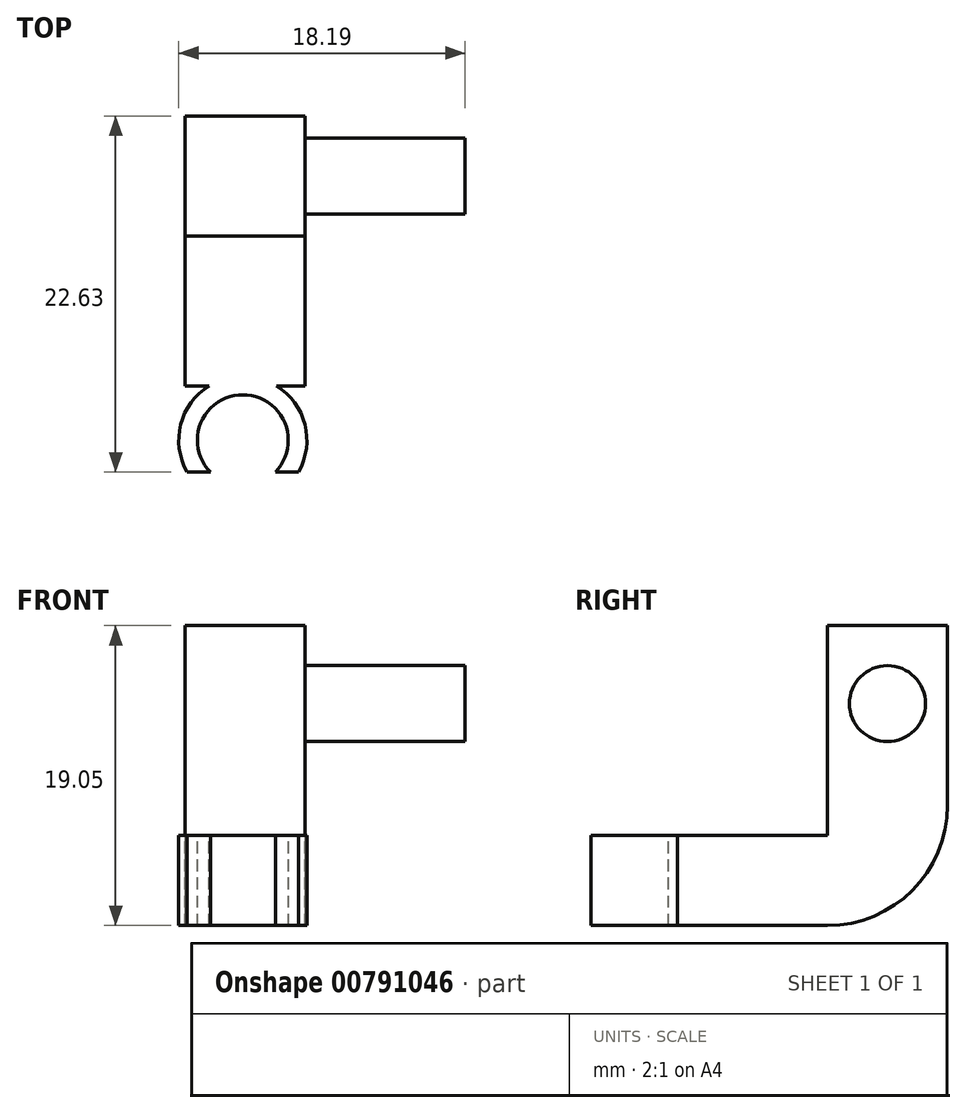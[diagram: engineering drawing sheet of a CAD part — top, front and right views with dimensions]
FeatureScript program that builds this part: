
annotation { "Feature Type Name" : "Feature", "Feature Type Description" : "" }
export const myFeature = defineFeature(function(context is Context, id is Id, definition is map)
    precondition{}
    {
        {
            var Q0;
            Q0=qCreatedBy(makeId("Front.planeOp"),FACE);
            var sketch = newSketch(context, id + "F0", { "sketchPlane" : qUnion([Q0])});
            skLineSegment(sketch, "E0.bottom", {"start": v(0, 26.58) * mm, "end": v(5.08, 26.58) * mm});
            skLineSegment(sketch, "E0.top", {"start": v(0, 13.88) * mm, "end": v(5.08, 13.88) * mm});
            skLineSegment(sketch, "E0.left", {"start": v(0, 26.58) * mm, "end": v(0, 13.88) * mm});
            skLineSegment(sketch, "E0.right", {"start": v(5.08, 26.58) * mm, "end": v(5.08, 13.88) * mm});
            skSolve(sketch);
        }
        {
            var Q0;
            Q0 = qSketchRegion(id + "F0", true);
            extrude(context, id + "F1", {"entities" : qUnion([Q0]), "depth" : 5.08 * mm, "offsetDistance" : 25.4 * mm});
        }
        {
            var Q0;
            Q0=makeQuery(id+"F1.opExtrude","CAP_FACE",FACE,{"disambiguationData":[OSD([sQuery(id+"F0.wireOp",EDGE,"E0.bottom"),sQuery(id+"F0.wireOp",EDGE,"E0.top"),sQuery(id+"F0.wireOp",EDGE,"E0.left"),sQuery(id+"F0.wireOp",EDGE,"E0.right")])],"isStart":false});
            var sketch = newSketch(context, id + "F2", { "sketchPlane" : qUnion([Q0])});
            skLineSegment(sketch, "E1.bottom", {"start": v(0, 13.88) * mm, "end": v(5.08, 13.88) * mm});
            skLineSegment(sketch, "E1.top", {"start": v(0, 17.69) * mm, "end": v(5.08, 17.69) * mm});
            skLineSegment(sketch, "E1.left", {"start": v(0, 13.88) * mm, "end": v(0, 17.69) * mm});
            skLineSegment(sketch, "E1.right", {"start": v(5.08, 13.88) * mm, "end": v(5.08, 17.69) * mm});
            skSolve(sketch);
        }
        {
            var Q0;
            Q0 = qSketchRegion(id + "F2", true);
            extrude(context, id + "F3", {"entities" : qUnion([Q0]), "operationType" : NewBodyOperationType.ADD, "depth" : 6.35 * mm, "offsetDistance" : 25.4 * mm});
        }
        {
            var Q0;
            Q0=makeQuery(id+"F1.opExtrude","CAP_EDGE",EDGE,{"disambiguationData":[OSD([sQuery(id+"F0.wireOp",EDGE,"E0.top")])],"isStart":true});
            fillet(context, id + "F4", {"entities" : qUnion([Q0]), "radius" : 5.08 * mm, "tangentPropagation" : true, "allowEdgeOverflow" : false});
        }
        {
            var Q0;
            Q0=makeQuery(id+"F3.opExtrude","SWEPT_FACE",FACE,{"disambiguationData":[OSD([sQuery(id+"F2.wireOp",EDGE,"E1.top")])]});
            var sketch = newSketch(context, id + "F5", { "sketchPlane" : qUnion([Q0])});
            skCircle(sketch, "E2", {"center": v(2.44, -13.74) * mm, "radius": 2.71 * mm});
            skPoint(sketch, "E2.first.point", {"position": v(2.54, -11.03) * mm});
            skPoint(sketch, "E2.first.point.positionSnap0", {"position": v(2.54, -11.43) * mm});
            skPoint(sketch, "E2.second.point", {"position": v(2.1, -16.43) * mm});
            skPoint(sketch, "E2.third.point", {"position": v(3.02, -16.39) * mm});
            skSolve(sketch);
        }
        {
            var Q0;
            Q0 = qSketchRegion(id + "F5", true);
            extrude(context, id + "F6", {"entities" : qUnion([Q0]), "operationType" : NewBodyOperationType.ADD, "oppositeDirection" : true, "depth" : 3.8 * mm, "offsetDistance" : 25.4 * mm});
        }
        {
            var Q0;
            Q0=makeQuery(id+"F6.boolean.opBoolean","MERGE",FACE,{"derivedFrom":[makeQuery(id+"F3.opExtrude","SWEPT_FACE",FACE,{"disambiguationData":[OSD([sQuery(id+"F2.wireOp",EDGE,"E1.top")])]}),makeQuery(id+"F6.opExtrude","CAP_FACE",FACE,{"disambiguationData":[OSD([sQuery(id+"F5.wireOp",EDGE,"E2")])],"isStart":true})]});
            var sketch = newSketch(context, id + "F7", { "sketchPlane" : qUnion([Q0])});
            skCircle(sketch, "E3", {"center": v(2.44, -13.74) * mm, "radius": 1.93 * mm});
            skSolve(sketch);
        }
        {
            var Q0;
            Q0 = qSketchRegion(id + "F7", true);
            extrude(context, id + "F8", {"entities" : qUnion([Q0]), "operationType" : NewBodyOperationType.REMOVE, "oppositeDirection" : true, "depth" : 3.8 * mm, "offsetDistance" : 25.4 * mm});
        }
        {
            var Q0;
            Q0=makeQuery(id+"F6.boolean.opBoolean","MERGE",FACE,{"derivedFrom":[makeQuery(id+"F3.opExtrude","SWEPT_FACE",FACE,{"disambiguationData":[OSD([sQuery(id+"F2.wireOp",EDGE,"E1.top")])]}),makeQuery(id+"F6.opExtrude","CAP_FACE",FACE,{"disambiguationData":[OSD([sQuery(id+"F5.wireOp",EDGE,"E2")])],"isStart":true})]});
            var sketch = newSketch(context, id + "F9", { "sketchPlane" : qUnion([Q0])});
            skLineSegment(sketch, "E4.bottom", {"start": v(0.08, -15.08) * mm, "end": v(5.44, -15.08) * mm});
            skLineSegment(sketch, "E4.top", {"start": v(0.08, -16.71) * mm, "end": v(5.44, -16.71) * mm});
            skLineSegment(sketch, "E4.left", {"start": v(0.08, -15.08) * mm, "end": v(0.08, -16.71) * mm});
            skLineSegment(sketch, "E4.right", {"start": v(5.44, -15.08) * mm, "end": v(5.44, -16.71) * mm});
            skSolve(sketch);
        }
        {
            var Q0;
            Q0 = qSketchRegion(id + "F9", true);
            extrude(context, id + "F10", {"entities" : qUnion([Q0]), "operationType" : NewBodyOperationType.REMOVE, "oppositeDirection" : true, "depth" : 3.8 * mm, "offsetDistance" : 25.4 * mm});
        }
        {
            var Q0;
            Q0=makeQuery(id+"F1.opExtrude","SWEPT_BODY",BODY,{"disambiguationData":[OSD([sQuery(id+"F0.wireOp",EDGE,"E0.bottom"),sQuery(id+"F0.wireOp",EDGE,"E0.top"),sQuery(id+"F0.wireOp",EDGE,"E0.left"),sQuery(id+"F0.wireOp",EDGE,"E0.right")])]});
            var Q1;
            Q1=qCreatedBy(makeId("Origin.pointOp"),VERTEX);
            transform(context, id + "F11", {"entities" : qUnion([Q0]), "transformType" : TransformType.SCALE_UNIFORMLY, "scale" : 1.5, "scalePoint" : qUnion([Q1]), "makeCopy" : false});
        }
        {
            var Q0;
            Q0=makeQuery(id+"F3.boolean.opBoolean","MERGE",FACE,{"derivedFrom":[makeQuery(id+"F1.opExtrude","SWEPT_FACE",FACE,{"disambiguationData":[OSD([sQuery(id+"F0.wireOp",EDGE,"E0.right")])]}),makeQuery(id+"F3.opExtrude","SWEPT_FACE",FACE,{"disambiguationData":[OSD([sQuery(id+"F2.wireOp",EDGE,"E1.right")])]})]});
            var sketch = newSketch(context, id + "F12", { "sketchPlane" : qUnion([Q0])});
            skCircle(sketch, "E5", {"center": v(-3.81, 34.92) * mm, "radius": 2.41 * mm});
            skPoint(sketch, "E5.centerSnap0", {"position": v(-3.81, 39.87) * mm});
            skSolve(sketch);
        }
        {
            var Q0;
            Q0=makeQuery(id+"F12.imprint","IMPRINT",FACE,{"disambiguationData":[TD([[makeQuery(id+"F12.imprint","IMPRINT",EDGE,{"derivedFrom":sQuery(id+"F12.wireOp",EDGE,"E5")}),1.0]])]});
            extrude(context, id + "F13", {"entities" : qUnion([Q0]), "operationType" : NewBodyOperationType.ADD, "depth" : 10.16 * mm, "offsetDistance" : 25.4 * mm});
        }
    });
